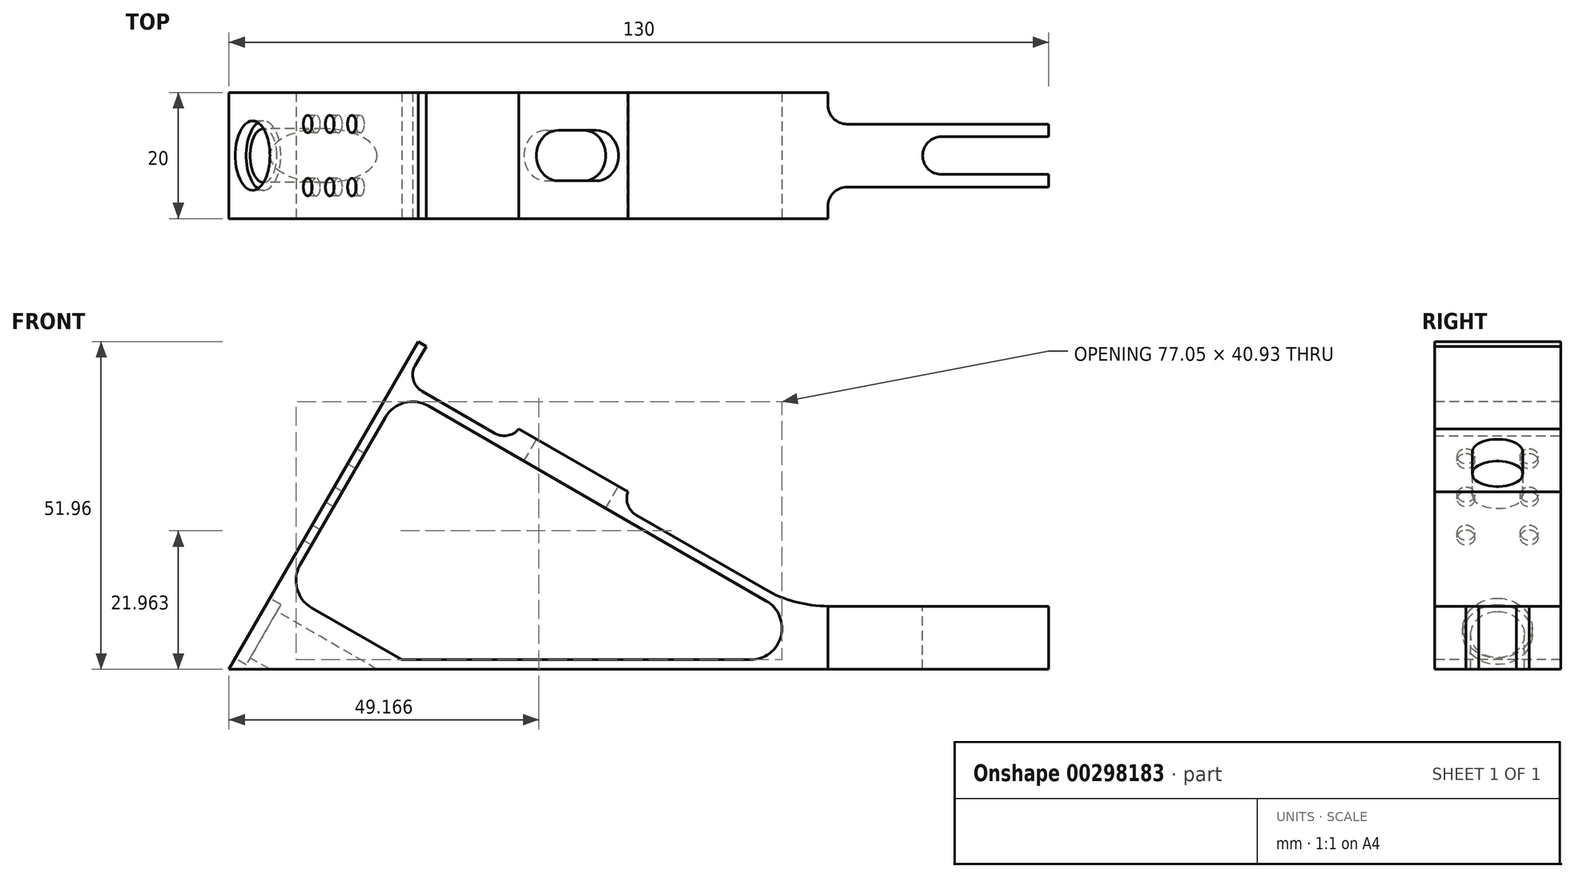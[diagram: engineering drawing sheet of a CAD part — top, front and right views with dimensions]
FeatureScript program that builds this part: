
annotation { "Feature Type Name" : "Feature", "Feature Type Description" : "" }
export const myFeature = defineFeature(function(context is Context, id is Id, definition is map)
    precondition{}
    {
        {
            var Q0;
            Q0=qCreatedBy(makeId("Front.planeOp"),FACE);
            var sketch = newSketch(context, id + "F0", { "sketchPlane" : qUnion([Q0])});
            skLineSegment(sketch, "E0", {"start": v(0, 0) * mm, "end": v(30, 51.96) * mm});
            skLineSegment(sketch, "E1", {"start": v(0, 0) * mm, "end": v(130, 0) * mm});
            skLineSegment(sketch, "E2", {"start": v(30, 51.96) * mm, "end": v(31.3, 51.21) * mm});
            skLineSegment(sketch, "E3", {"start": v(130, 0) * mm, "end": v(130, 10) * mm});
            skLineSegment(sketch, "E4", {"start": v(130, 10) * mm, "end": v(95, 10) * mm});
            skLineSegment(sketch, "E5", {"start": v(28.04, 45.57) * mm, "end": v(44.71, 35.94) * mm});
            skLineSegment(sketch, "E6", {"start": v(44.71, 35.94) * mm, "end": v(45.96, 38.1) * mm});
            skLineSegment(sketch, "E7", {"start": v(45.96, 38.1) * mm, "end": v(63.28, 28.1) * mm});
            skLineSegment(sketch, "E8", {"start": v(63.28, 28.1) * mm, "end": v(62.03, 25.94) * mm});
            skLineSegment(sketch, "E9", {"start": v(62.03, 25.94) * mm, "end": v(85, 12.68) * mm});
            skArc(sketch, "E10", {"start": v(85, 12.68) * mm, "mid": v(89.82, 10.68) * mm, "end": v(95, 10) * mm});
            skLineSegment(sketch, "E11", {"start": v(31.3, 51.21) * mm, "end": v(28.04, 45.57) * mm});
            skSolve(sketch);
        }
        {
            var Q0;
            Q0 = qSketchRegion(id + "F0", true);
            extrude(context, id + "F1", {"entities" : qUnion([Q0]), "endBound" : BoundingType.SYMMETRIC, "depth" : 20 * mm});
        }
        {
            var Q0;
            Q0=makeQuery(id+"F1.opExtrude","SWEPT_EDGE",EDGE,{"disambiguationData":[OSD([sQuery(id+"F0.wireOp",EDGE,"VtlEid7S-QaKo-K9HM-9ov8-MFXf0RC3C2EM"),sQuery(id+"F0.wireOp",EDGE,"E5")])]});
            var Q1;
            Q1=makeQuery(id+"F1.opExtrude","SWEPT_EDGE",EDGE,{"disambiguationData":[OSD([sQuery(id+"F0.wireOp",EDGE,"E8"),sQuery(id+"F0.wireOp",EDGE,"E9")])]});
            var Q2;
            Q2=makeQuery(id+"F1.opExtrude","SWEPT_EDGE",EDGE,{"disambiguationData":[OSD([sQuery(id+"F0.wireOp",EDGE,"E5"),sQuery(id+"F0.wireOp",EDGE,"E6")])]});
            fillet(context, id + "F2", {"entities" : qUnion([Q0, Q1, Q2]), "radius" : 3 * mm, "tangentPropagation" : true, "allowEdgeOverflow" : false});
        }
        {
            var Q0;
            Q0=makeQuery(id+"F1.opExtrude","CAP_FACE",FACE,{"disambiguationData":[OSD([sQuery(id+"F0.wireOp",EDGE,"E0"),sQuery(id+"F0.wireOp",EDGE,"E1"),sQuery(id+"F0.wireOp",EDGE,"E2"),sQuery(id+"F0.wireOp",EDGE,"E3"),sQuery(id+"F0.wireOp",EDGE,"E4"),sQuery(id+"F0.wireOp",EDGE,"VtlEid7S-QaKo-K9HM-9ov8-MFXf0RC3C2EM"),sQuery(id+"F0.wireOp",EDGE,"E5"),sQuery(id+"F0.wireOp",EDGE,"E6"),sQuery(id+"F0.wireOp",EDGE,"E7"),sQuery(id+"F0.wireOp",EDGE,"E8"),sQuery(id+"F0.wireOp",EDGE,"E9"),sQuery(id+"F0.wireOp",EDGE,"E10")])],"isStart":false});
            var sketch = newSketch(context, id + "F3", { "sketchPlane" : qUnion([Q0])});
            skArc(sketch, "E12", {"start": v(85.2, 10.83) * mm, "mid": v(87.53, 5.2) * mm, "end": v(82.7, 1.5) * mm});
            skLineSegment(sketch, "E13", {"start": v(85.2, 10.83) * mm, "end": v(31.62, 41.77) * mm});
            skLineSegment(sketch, "E14", {"start": v(82.7, 1.5) * mm, "end": v(27.4, 1.5) * mm});
            skLineSegment(sketch, "E15", {"start": v(27.4, 1.5) * mm, "end": v(13.13, 9.74) * mm});
            skLineSegment(sketch, "E16", {"start": v(24.79, 39.94) * mm, "end": v(11.3, 16.57) * mm});
            skArc(sketch, "E17", {"start": v(31.62, 41.77) * mm, "mid": v(27.83, 42.27) * mm, "end": v(24.79, 39.94) * mm});
            skArc(sketch, "E18", {"start": v(11.3, 16.57) * mm, "mid": v(10.8, 12.78) * mm, "end": v(13.13, 9.74) * mm});
            skSolve(sketch);
        }
        {
            var Q0;
            Q0 = qSketchRegion(id + "F3", true);
            extrude(context, id + "F4", {"entities" : qUnion([Q0]), "operationType" : NewBodyOperationType.REMOVE, "endBound" : BoundingType.THROUGH_ALL, "oppositeDirection" : true, "depth" : 25 * mm});
        }
        {
            var Q0;
            Q0=makeQuery(id+"F1.opExtrude","SWEPT_FACE",FACE,{"disambiguationData":[OSD([sQuery(id+"F0.wireOp",EDGE,"E4")])]});
            var sketch = newSketch(context, id + "F5", { "sketchPlane" : qUnion([Q0])});
            skLineSegment(sketch, "E19", {"start": v(130, 0) * mm, "end": v(71.95, 0) * mm, "construction": true});
            skLineSegment(sketch, "E20.bottom", {"start": v(130, 10) * mm, "end": v(95, 10) * mm});
            skLineSegment(sketch, "E20.top", {"start": v(130, 5) * mm, "end": v(95, 5) * mm});
            skLineSegment(sketch, "E20.left", {"start": v(130, 10) * mm, "end": v(130, 5) * mm});
            skLineSegment(sketch, "E20.right", {"start": v(95, 10) * mm, "end": v(95, 5) * mm});
            skLineSegment(sketch, "E21.MirrorCS", {"start": v(130, -5) * mm, "end": v(95, -5) * mm});
            skLineSegment(sketch, "E22.MirrorCS", {"start": v(130, -10) * mm, "end": v(95, -10) * mm});
            skLineSegment(sketch, "E23.MirrorCS", {"start": v(130, -10) * mm, "end": v(130, -5) * mm});
            skLineSegment(sketch, "E24.MirrorCS", {"start": v(95, -10) * mm, "end": v(95, -5) * mm});
            skSolve(sketch);
        }
        {
            var Q0;
            Q0=makeQuery(id+"F5.imprint","IMPRINT",FACE,{"disambiguationData":[TD([[makeQuery(id+"F5.imprint","IMPRINT",EDGE,{"derivedFrom":sQuery(id+"F5.wireOp",EDGE,"E20.bottom")}),1.0]])]});
            var Q1;
            Q1=makeQuery(id+"F5.imprint","IMPRINT",FACE,{"disambiguationData":[TD([[makeQuery(id+"F5.imprint","IMPRINT",EDGE,{"derivedFrom":sQuery(id+"F5.wireOp",EDGE,"E21.MirrorCS")}),1.0]])]});
            extrude(context, id + "F6", {"entities" : qUnion([Q0, Q1]), "operationType" : NewBodyOperationType.REMOVE, "endBound" : BoundingType.THROUGH_ALL, "oppositeDirection" : true, "depth" : 25 * mm});
        }
        {
            var Q0;
            Q0=makeQuery(id+"F6.boolean.opBoolean","COPY",EDGE,{"derivedFrom":makeQuery(id+"F6.opExtrude","SWEPT_EDGE",EDGE,{"disambiguationData":[OSD([sQuery(id+"F0.wireOp",EDGE,"E4"),sQuery(id+"F0.wireOp",EDGE,"E10"),sQuery(id+"F5.wireOp",EDGE,"E21.MirrorCS"),sQuery(id+"F5.wireOp",EDGE,"E24.MirrorCS")])]})});
            var Q1;
            Q1=makeQuery(id+"F6.boolean.opBoolean","COPY",EDGE,{"derivedFrom":makeQuery(id+"F6.opExtrude","SWEPT_EDGE",EDGE,{"disambiguationData":[OSD([sQuery(id+"F0.wireOp",EDGE,"E4"),sQuery(id+"F0.wireOp",EDGE,"E10"),sQuery(id+"F5.wireOp",EDGE,"E20.top"),sQuery(id+"F5.wireOp",EDGE,"E20.right")])]})});
            fillet(context, id + "F7", {"entities" : qUnion([Q0, Q1]), "radius" : 3 * mm, "tangentPropagation" : true, "allowEdgeOverflow" : false});
        }
        {
            var Q0;
            Q0=makeQuery(id+"F1.opExtrude","SWEPT_FACE",FACE,{"disambiguationData":[OSD([sQuery(id+"F0.wireOp",EDGE,"E4")])]});
            var sketch = newSketch(context, id + "F8", { "sketchPlane" : qUnion([Q0])});
            skLineSegment(sketch, "E25", {"start": v(130, 3) * mm, "end": v(113, 3) * mm});
            skLineSegment(sketch, "E26", {"start": v(130, -3) * mm, "end": v(113, -3) * mm});
            skArc(sketch, "E27", {"start": v(113, 3) * mm, "mid": v(110, 0) * mm, "end": v(113, -3) * mm});
            skSolve(sketch);
        }
        {
            var Q0;
            Q0 = qSketchRegion(id + "F8", true);
            var Q1;
            {var subQ0=sQuery(id+"F8.wireOp",EDGE,"E25");Q1=makeQuery(id+"F8.imprint","IMPRINT",FACE,{"disambiguationData":[TD([[makeQuery(id+"F8.imprint","IMPRINT",EDGE,{"derivedFrom":subQ0}),1.0]])]});}
            extrude(context, id + "F9", {"entities" : qUnion([Q0, Q1]), "operationType" : NewBodyOperationType.REMOVE, "endBound" : BoundingType.THROUGH_ALL, "oppositeDirection" : true, "depth" : 25 * mm});
        }
        {
            var Q0;
            Q0=makeQuery(id+"F1.opExtrude","SWEPT_FACE",FACE,{"disambiguationData":[OSD([sQuery(id+"F0.wireOp",EDGE,"E7")])]});
            var sketch = newSketch(context, id + "F10", { "sketchPlane" : qUnion([Q0])});
            skLineSegment(sketch, "E28", {"start": v(0, 0) * mm, "end": v(50.7, 0) * mm, "construction": true});
            skLineSegment(sketch, "E29", {"start": v(28, 4) * mm, "end": v(35, 4) * mm});
            skLineSegment(sketch, "E30", {"start": v(28, -4) * mm, "end": v(35, -4) * mm});
            skArc(sketch, "E31", {"start": v(28, 4) * mm, "mid": v(24, 0) * mm, "end": v(28, -4) * mm});
            skArc(sketch, "E32", {"start": v(35, 4) * mm, "mid": v(39, 0) * mm, "end": v(35, -4) * mm});
            skSolve(sketch);
        }
        {
            var Q0;
            Q0=makeQuery(id+"F10.imprint","IMPRINT",FACE,{"disambiguationData":[TD([[makeQuery(id+"F10.imprint","IMPRINT",EDGE,{"derivedFrom":sQuery(id+"F10.wireOp",EDGE,"E29")}),-1.0]])]});
            extrude(context, id + "F11", {"entities" : qUnion([Q0]), "operationType" : NewBodyOperationType.REMOVE, "oppositeDirection" : true, "depth" : 4 * mm});
        }
        {
            var Q0;
            Q0=makeQuery(id+"F1.opExtrude","SWEPT_FACE",FACE,{"disambiguationData":[OSD([sQuery(id+"F0.wireOp",EDGE,"E0")])]});
            var sketch = newSketch(context, id + "F12", { "sketchPlane" : qUnion([Q0])});
            skCircle(sketch, "E33", {"center": v(0, 7.5) * mm, "radius": 5.5 * mm});
            skSolve(sketch);
        }
        {
            var Q0;
            Q0=makeQuery(id+"F12.imprint","IMPRINT",FACE,{"disambiguationData":[TD([[makeQuery(id+"F12.imprint","IMPRINT",EDGE,{"derivedFrom":sQuery(id+"F12.wireOp",EDGE,"E33")}),1.0]])]});
            extrude(context, id + "F13", {"entities" : qUnion([Q0]), "operationType" : NewBodyOperationType.REMOVE, "oppositeDirection" : true, "depth" : 2 * mm});
        }
        {
            var Q0;
            Q0=makeQuery(id+"F1.opExtrude","SWEPT_FACE",FACE,{"disambiguationData":[OSD([sQuery(id+"F0.wireOp",EDGE,"E0")])]});
            var sketch = newSketch(context, id + "F14", { "sketchPlane" : qUnion([Q0])});
            skCircle(sketch, "E34", {"center": v(0, 7.5) * mm, "radius": 4.25 * mm});
            skSolve(sketch);
        }
        {
            var Q0;
            Q0 = qSketchRegion(id + "F14", true);
            extrude(context, id + "F15", {"entities" : qUnion([Q0]), "operationType" : NewBodyOperationType.REMOVE, "endBound" : BoundingType.THROUGH_ALL, "oppositeDirection" : true, "depth" : 25 * mm});
        }
        {
            var Q0;
            Q0=makeQuery(id+"F1.opExtrude","SWEPT_FACE",FACE,{"disambiguationData":[OSD([sQuery(id+"F0.wireOp",EDGE,"E0")])]});
            var sketch = newSketch(context, id + "F16", { "sketchPlane" : qUnion([Q0])});
            skCircle(sketch, "E35", {"center": v(-5, 25) * mm, "radius": 1.4 * mm});
            skCircle(sketch, "E36", {"center": v(-5, 32) * mm, "radius": 1.4 * mm});
            skCircle(sketch, "E37", {"center": v(-5, 39) * mm, "radius": 1.4 * mm});
            skCircle(sketch, "E38", {"center": v(5, 39) * mm, "radius": 1.4 * mm});
            skCircle(sketch, "E39", {"center": v(5, 32) * mm, "radius": 1.4 * mm});
            skCircle(sketch, "E40", {"center": v(5, 25) * mm, "radius": 1.4 * mm});
            skSolve(sketch);
        }
        {
            var Q0;
            Q0 = qSketchRegion(id + "F16", true);
            extrude(context, id + "F17", {"entities" : qUnion([Q0]), "operationType" : NewBodyOperationType.REMOVE, "oppositeDirection" : true, "depth" : 25 * mm});
        }
    });
